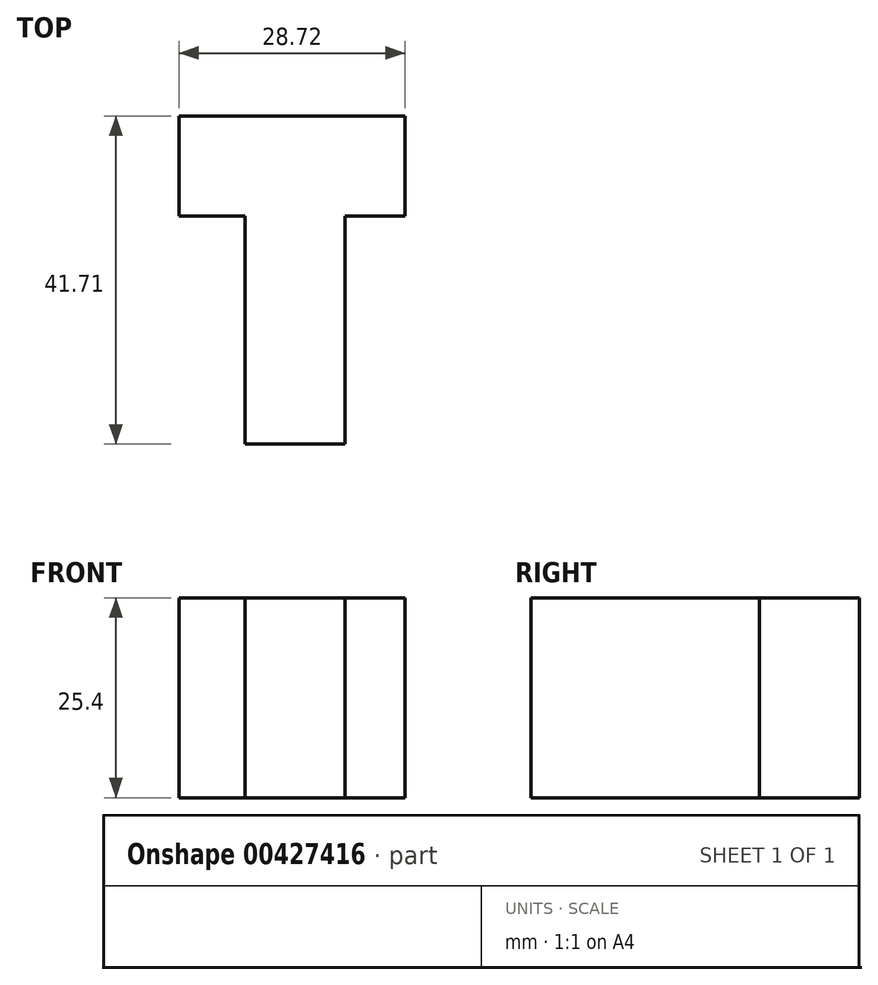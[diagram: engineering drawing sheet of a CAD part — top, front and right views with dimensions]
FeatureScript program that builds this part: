
annotation { "Feature Type Name" : "Feature", "Feature Type Description" : "" }
export const myFeature = defineFeature(function(context is Context, id is Id, definition is map)
    precondition{}
    {
        {
            var Q0;
            Q0=qCreatedBy(makeId("Top.planeOp"),FACE);
            var sketch = newSketch(context, id + "F0", { "sketchPlane" : qUnion([Q0])});
            skLineSegment(sketch, "E0", {"start": v(0, 0) * mm, "end": v(12.7, 0) * mm});
            skLineSegment(sketch, "E1", {"start": v(12.7, 0) * mm, "end": v(12.7, 29) * mm});
            skLineSegment(sketch, "E2", {"start": v(12.7, 29) * mm, "end": v(20.32, 29) * mm});
            skLineSegment(sketch, "E3", {"start": v(20.32, 29) * mm, "end": v(20.32, 41.7) * mm});
            skLineSegment(sketch, "E4", {"start": v(20.32, 41.7) * mm, "end": v(-8.4, 41.7) * mm});
            skLineSegment(sketch, "E5", {"start": v(-8.4, 41.7) * mm, "end": v(-8.4, 29) * mm});
            skLineSegment(sketch, "E6", {"start": v(-8.4, 29) * mm, "end": v(0, 29) * mm});
            skLineSegment(sketch, "E7", {"start": v(0, 29) * mm, "end": v(0, 0) * mm});
            skSolve(sketch);
        }
        {
            var Q0;
            Q0 = qSketchRegion(id + "F0", true);
            extrude(context, id + "F1", {"entities" : qUnion([Q0]), "depth" : 25.4 * mm});
        }
    });
